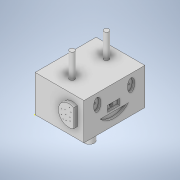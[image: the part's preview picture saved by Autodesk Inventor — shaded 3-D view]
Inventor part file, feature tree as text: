
AUTODESK INVENTOR PART (.ipt)
format: ipt  version: 2021 (Build 250183000, 183)  size: 233,472 bytes
history: native  units: mm
features: sketch x32, hole x21, extrude x11
ambient origin geometry x8: Origin, YZ Plane, XZ Plane, XY Plane, X Axis, Y Axis, Z Axis, Center Point
bodies: Solid1 (feature_tree)
feature tree (64):
  extrude  "Extrusion1"  Depth=10.0mm TaperAngle=0.0deg
  sketch  "Sketch2"  dims[d6=10.0mm d7=0.0mm d8=10.0mm d9=0.0mm]
  sketch  "Sketch3"  dims[d10=15.0mm d11=0.0mm d12=15.0mm d13=0.0mm]
  extrude  "Extrusion2"  Depth=10.0mm TaperAngle=0.0deg
  extrude  "Extrusion3"  Depth=15.0mm TaperAngle=0.0deg
  extrude  "Extrusion4"  Depth=20.0mm
  extrude  "Extrusion5"  Depth=100.0mm TaperAngle=0.0deg
  extrude  "Extrusion6"  Depth=100.0mm TaperAngle=0.0deg
  sketch  "Sketch6"  dims[d20=40.0mm d21=100.0mm d22=0.0mm]
  extrude  "Extrusion7"  Depth=50.0mm
  extrude  "Extrusion8"  Depth=10.0mm TaperAngle=0.0deg
  sketch  "Sketch7"  dims[d23=2.0mm d24=6.0mm d25=3.023mm d26=2.0mm d27=14.3117mm d28=5.0mm d29=20.594885mm]
  sketch  "Sketch8"  dims[d30=2.0mm d31=6.0mm d32=3.023mm d33=2.0mm d34=14.3117mm d35=5.0mm d36=20.594885mm]
  extrude  "Extrusion9"  Depth=50.0mm TaperAngle=0.0deg
  hole  "Hole1"  [1 undecoded]
  hole  "Hole2"  [1 undecoded]
  hole  "Hole3"  [1 undecoded]
  hole  "Hole4"  [1 undecoded]
  hole  "Hole5"  [1 undecoded]
  hole  "Hole6"  [1 undecoded]
  hole  "Hole7"  [1 undecoded]
  hole  "Hole8"  [1 undecoded]
  hole  "Hole9"  [1 undecoded]
  hole  "Hole10"  [1 undecoded]
  hole  "Hole11"  [1 undecoded]
  hole  "Hole12"  [1 undecoded]
  hole  "Hole13"  [1 undecoded]
  hole  "Hole14"  [1 undecoded]
  hole  "Hole15"  [1 undecoded]
  hole  "Hole16"  [1 undecoded]
  hole  "Hole17"  [1 undecoded]
  hole  "Hole18"  [1 undecoded]
  hole  "Hole19"  [1 undecoded]
  extrude  "Extrusion10"  [1 undecoded]
  extrude  "Extrusion11"  [1 undecoded]
  hole  "Hole20"  [1 undecoded]
  hole  "Hole21"  [1 undecoded]
  sketch  "Sketch1"  dims[d2=200.0mm d3=0.0mm d4=10.0mm d5=0.0mm]
  sketch  "Sketch4"  dims[d14=20.0mm d15=20.0mm]
  sketch  "Sketch5"  dims[d16=100.0mm d17=0.0mm d18=100.0mm d19=0.0mm]
  sketch  "Sketch9"  dims[d37=2.0mm d38=6.0mm d39=3.023mm d40=2.0mm d41=14.3117mm d42=5.0mm d43=20.594885mm]
  sketch  "Sketch10"  dims[d44=2.0mm d45=6.0mm d46=3.023mm d47=2.0mm d48=14.3117mm d49=5.0mm d50=20.594885mm]
  sketch  "Sketch11"  dims[d51=2.0mm d52=6.0mm d53=3.023mm d54=2.0mm d55=14.3117mm d56=5.0mm d57=20.594885mm]
  sketch  "Sketch12"  dims[d58=2.0mm d59=6.0mm d60=3.023mm d61=2.0mm d62=14.3117mm d63=5.0mm d64=20.594885mm]
  sketch  "Sketch13"  dims[d65=2.0mm d66=6.0mm d67=3.023mm d68=2.0mm d69=14.3117mm d70=5.0mm d71=20.594885mm]
  sketch  "Sketch14"  dims[d72=2.0mm d73=6.0mm d74=3.023mm d75=2.0mm d76=14.3117mm d77=5.0mm d78=20.594885mm]
  sketch  "Sketch15"  dims[d79=2.0mm d80=6.0mm d81=3.023mm d82=2.0mm d83=14.3117mm d84=5.0mm d85=20.594885mm]
  sketch  "Sketch16"  dims[d86=2.0mm d87=6.0mm d88=3.023mm d89=2.0mm d90=14.3117mm d91=5.0mm d92=20.594885mm]
  sketch  "Sketch17"  dims[d93=2.0mm d94=6.0mm d95=3.023mm d96=2.0mm d97=14.3117mm d98=5.0mm d99=20.594885mm]
  sketch  "Sketch18"  dims[d100=2.0mm d101=6.0mm d102=3.023mm d103=2.0mm d104=14.3117mm d105=5.0mm d106=20.594885mm]
  sketch  "Sketch19"  dims[d107=2.0mm d108=6.0mm d109=3.023mm d110=2.0mm d111=14.3117mm d112=5.0mm d113=20.594885mm]
  sketch  "Sketch20"  dims[d114=2.0mm d115=6.0mm d116=3.023mm d117=2.0mm d118=14.3117mm d119=5.0mm d120=20.594885mm]
  sketch  "Sketch21"  dims[d121=2.0mm d122=6.0mm d123=3.023mm d124=2.0mm d125=14.3117mm d126=5.0mm d127=20.594885mm]
  sketch  "Sketch22"  dims[d128=2.0mm d129=6.0mm d130=3.023mm d131=2.0mm d132=14.3117mm d133=5.0mm d134=20.594885mm]
  sketch  "Sketch23"  dims[d135=2.0mm d136=6.0mm d137=3.023mm d138=2.0mm d139=14.3117mm d140=5.0mm d141=20.594885mm]
  sketch  "Sketch24"  dims[d142=2.0mm d143=6.0mm d144=3.023mm d145=2.0mm d146=14.3117mm d147=5.0mm d148=20.594885mm]
  sketch  "Sketch25"  dims[d149=2.0mm d150=6.0mm d151=3.023mm d152=2.0mm d153=14.3117mm d154=5.0mm d155=20.594885mm d156=50.0mm]
  sketch  "Sketch26"  dims[d157=25.0mm d158=10.0mm d159=0.0mm]
  sketch  "Sketch27"  dims[d160=15.0mm d161=50.0mm d162=0.0mm]
  sketch  "Sketch28"  dims[d163=5.0mm d164=6.0mm d165=4.0mm d166=2.0mm d167=90.0deg d168=5.0mm d169=20.594885mm]
  sketch  "Sketch29"  dims[d170=5.0mm d171=6.0mm d172=4.0mm d173=2.0mm d174=90.0deg d175=5.0mm d176=20.594885mm]
  sketch  "Sketch30"
  sketch  "Sketch31"
  sketch  "Sketch32"
note: 23 required parameter values undecoded (feature->parameter linkage not recoverable at this tier; creation-order binding heuristic only, values carry confidence <= 0.55)
